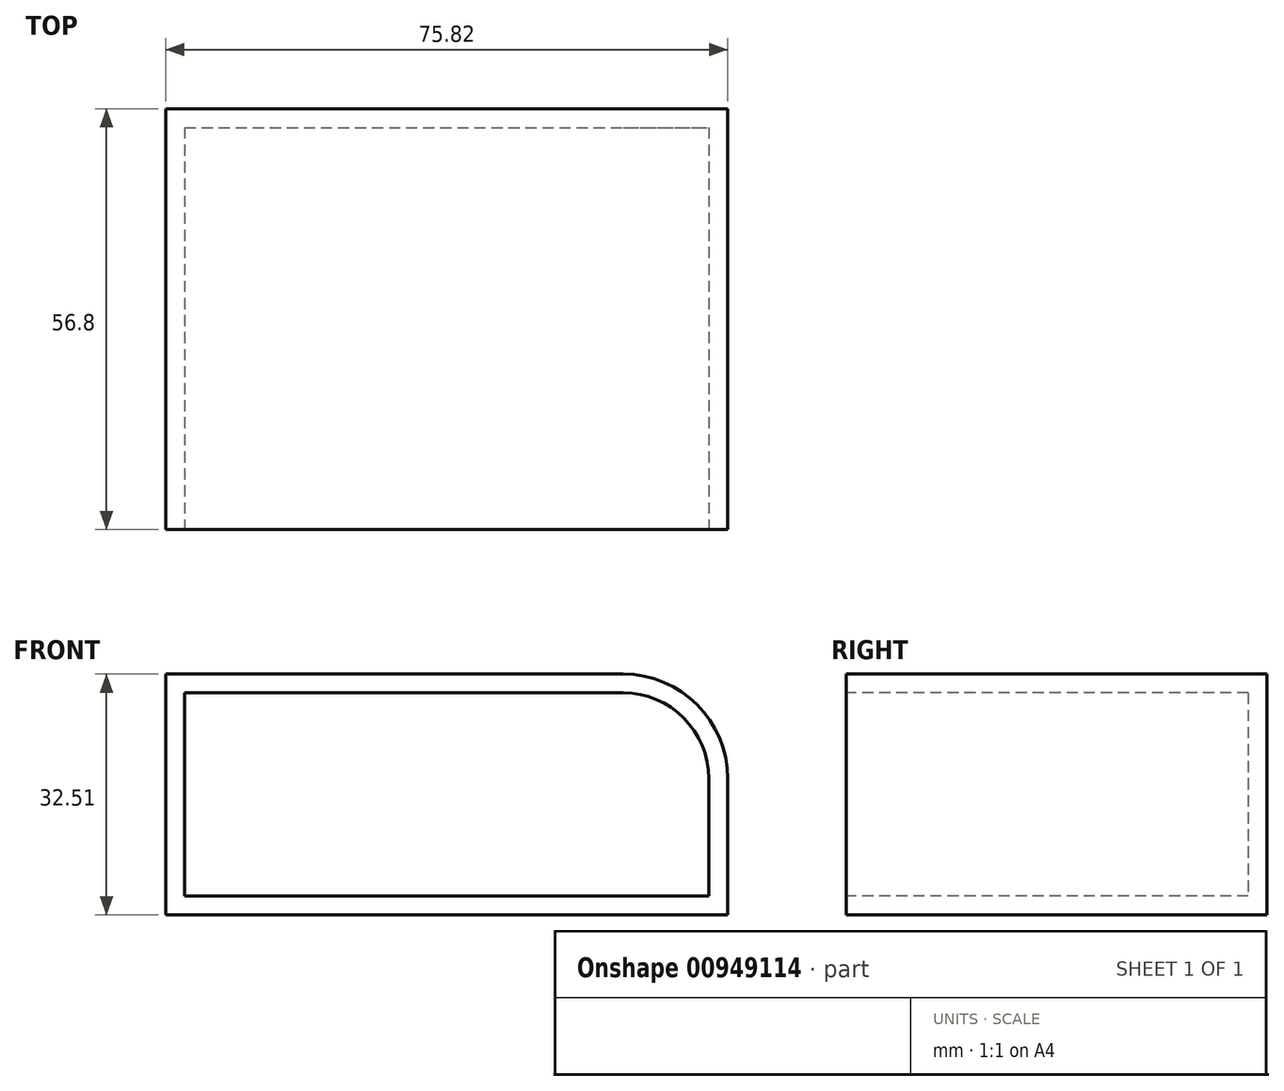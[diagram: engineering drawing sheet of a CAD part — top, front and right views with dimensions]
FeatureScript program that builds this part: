
annotation { "Feature Type Name" : "Feature", "Feature Type Description" : "" }
export const myFeature = defineFeature(function(context is Context, id is Id, definition is map)
    precondition{}
    {
        {
            var Q0;
            Q0=qCreatedBy(makeId("Top.planeOp"),FACE);
            var sketch = newSketch(context, id + "F0", { "sketchPlane" : qUnion([Q0])});
            skLineSegment(sketch, "E0.bottom", {"start": v(0, 0) * mm, "end": v(75.82, 0) * mm});
            skLineSegment(sketch, "E0.top", {"start": v(0, -56.8) * mm, "end": v(75.82, -56.8) * mm});
            skLineSegment(sketch, "E0.left", {"start": v(0, 0) * mm, "end": v(0, -56.8) * mm});
            skLineSegment(sketch, "E0.right", {"start": v(75.82, 0) * mm, "end": v(75.82, -56.8) * mm});
            skSolve(sketch);
        }
        {
            var Q0;
            Q0 = qSketchRegion(id + "F0", true);
            extrude(context, id + "F1", {"entities" : qUnion([Q0]), "depth" : 32.5 * mm, "offsetDistance" : 25.4 * mm});
        }
        {
            var Q0;
            Q0=makeQuery(id+"F1.opExtrude","CAP_EDGE",EDGE,{"disambiguationData":[OSD([sQuery(id+"F0.wireOp",EDGE,"E0.right")])],"isStart":false});
            fillet(context, id + "F2", {"entities" : qUnion([Q0]), "radius" : 14.1 * mm, "tangentPropagation" : true, "allowEdgeOverflow" : false});
        }
        {
            var Q0;
            Q0=makeQuery(id+"F1.opExtrude","SWEPT_FACE",FACE,{"disambiguationData":[OSD([sQuery(id+"F0.wireOp",EDGE,"E0.top")])]});
            shell(context, id + "F3", {"entities" : qUnion([Q0]), "thickness" : 2.54 * mm});
        }
    });
